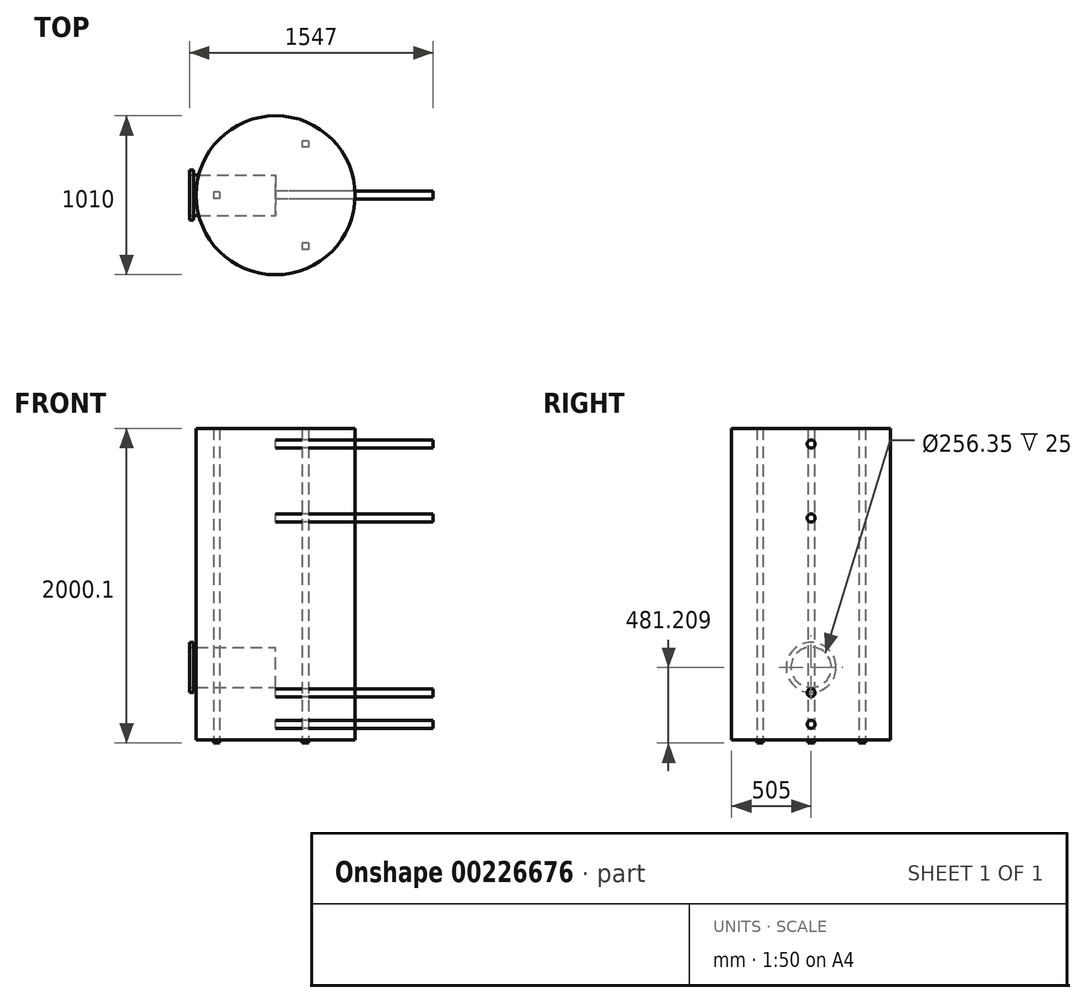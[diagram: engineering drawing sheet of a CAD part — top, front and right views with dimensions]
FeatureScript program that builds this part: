
annotation { "Feature Type Name" : "Feature", "Feature Type Description" : "" }
export const myFeature = defineFeature(function(context is Context, id is Id, definition is map)
    precondition{}
    {
        {
            var Q0;
            Q0=qCreatedBy(makeId("Top.planeOp"),FACE);
            var sketch = newSketch(context, id + "F0", { "sketchPlane" : qUnion([Q0])});
            skCircle(sketch, "E0", {"center": v(0, 0) * mm, "radius": 505 * mm});
            skPoint(sketch, "E1.0.midPoint", {"position": v(-93.82, -162.5) * mm});
            skLineSegment(sketch, "E2.bottom", {"start": v(207.64, -305) * mm, "end": v(167.64, -305) * mm});
            skLineSegment(sketch, "E2.top", {"start": v(207.64, -345) * mm, "end": v(167.64, -345) * mm});
            skLineSegment(sketch, "E2.left", {"start": v(207.64, -305) * mm, "end": v(207.64, -345) * mm});
            skLineSegment(sketch, "E2.right", {"start": v(167.64, -305) * mm, "end": v(167.64, -345) * mm});
            skPoint(sketch, "E2.middle", {"position": v(187.64, -325) * mm});
            skLineSegment(sketch, "E3.bottom", {"start": v(207.64, 345) * mm, "end": v(167.64, 345) * mm});
            skLineSegment(sketch, "E3.top", {"start": v(207.64, 305) * mm, "end": v(167.64, 305) * mm});
            skLineSegment(sketch, "E3.left", {"start": v(207.64, 345) * mm, "end": v(207.64, 305) * mm});
            skLineSegment(sketch, "E3.right", {"start": v(167.64, 345) * mm, "end": v(167.64, 305) * mm});
            skPoint(sketch, "E3.middle", {"position": v(187.64, 325) * mm});
            skLineSegment(sketch, "E4.bottom", {"start": v(-355.28, 20) * mm, "end": v(-395.28, 20) * mm});
            skLineSegment(sketch, "E4.top", {"start": v(-355.28, -20) * mm, "end": v(-395.28, -20) * mm});
            skLineSegment(sketch, "E4.left", {"start": v(-355.28, 20) * mm, "end": v(-355.28, -20) * mm});
            skLineSegment(sketch, "E4.right", {"start": v(-395.28, 20) * mm, "end": v(-395.28, -20) * mm});
            skPoint(sketch, "E4.middle", {"position": v(-375.28, 0) * mm});
            skSolve(sketch);
        }
        {
            var Q0;
            Q0=makeQuery(id+"F0.imprint","IMPRINT",FACE,{"disambiguationData":[TD([[makeQuery(id+"F0.imprint","IMPRINT",EDGE,{"derivedFrom":sQuery(id+"F0.wireOp",EDGE,"E0")}),1.0]])]});
            extrude(context, id + "F1", {"entities" : qUnion([Q0]), "depth" : 1980 * mm});
        }
        {
            var Q0;
            Q0=qCreatedBy(makeId("Right.planeOp"),FACE);
            var sketch = newSketch(context, id + "F2", { "sketchPlane" : qUnion([Q0])});
            skLineSegment(sketch, "E5", {"start": v(0, 0) * mm, "end": v(0, 100) * mm});
            skLineSegment(sketch, "E6", {"start": v(0, 100) * mm, "end": v(0, 300) * mm});
            skLineSegment(sketch, "E7", {"start": v(0, 300) * mm, "end": v(0, 1410) * mm});
            skLineSegment(sketch, "E8", {"start": v(0, 1410) * mm, "end": v(0, 1880) * mm});
            skCircle(sketch, "E9", {"center": v(0, 100) * mm, "radius": 25.4 * mm});
            skCircle(sketch, "E10", {"center": v(0, 300) * mm, "radius": 25.4 * mm});
            skCircle(sketch, "E11", {"center": v(0, 1410) * mm, "radius": 25.4 * mm});
            skCircle(sketch, "E12", {"center": v(0, 1880) * mm, "radius": 25.4 * mm});
            skCircle(sketch, "E13", {"center": v(0, 554.63) * mm, "radius": 129.58 * mm});
            skSolve(sketch);
        }
        {
            var Q0;
            {var subQ0=sQuery(id+"F2.wireOp",EDGE,"E6");var subQ1=sQuery(id+"F2.wireOp",EDGE,"E5");var subQ2=makeQuery(id+"F2.imprint","INTERSECT",VERTEX,{"derivedFrom":[subQ1,subQ0]});Q0=makeQuery(id+"F2.imprint","IMPRINT",FACE,{"disambiguationData":[TD([[makeQuery(id+"F2.imprint","IMPRINT",EDGE,{"disambiguationData":[TD([[subQ2,1.0]])],"derivedFrom":subQ1}),1.0]])]});}
            var Q1;
            {var subQ0=sQuery(id+"F2.wireOp",EDGE,"E6");var subQ1=sQuery(id+"F2.wireOp",EDGE,"E5");var subQ2=makeQuery(id+"F2.imprint","INTERSECT",VERTEX,{"derivedFrom":[subQ1,subQ0]});Q1=makeQuery(id+"F2.imprint","IMPRINT",FACE,{"disambiguationData":[TD([[makeQuery(id+"F2.imprint","IMPRINT",EDGE,{"disambiguationData":[TD([[subQ2,1.0]])],"derivedFrom":subQ1}),-1.0]])]});}
            var Q2;
            {var subQ0=sQuery(id+"F2.wireOp",EDGE,"E7");var subQ1=sQuery(id+"F2.wireOp",EDGE,"E6");var subQ2=makeQuery(id+"F2.imprint","INTERSECT",VERTEX,{"derivedFrom":[subQ1,subQ0]});Q2=makeQuery(id+"F2.imprint","IMPRINT",FACE,{"disambiguationData":[TD([[makeQuery(id+"F2.imprint","IMPRINT",EDGE,{"disambiguationData":[TD([[subQ2,1.0]])],"derivedFrom":subQ1}),1.0]])]});}
            var Q3;
            {var subQ0=sQuery(id+"F2.wireOp",EDGE,"E7");var subQ1=sQuery(id+"F2.wireOp",EDGE,"E6");var subQ2=makeQuery(id+"F2.imprint","INTERSECT",VERTEX,{"derivedFrom":[subQ1,subQ0]});Q3=makeQuery(id+"F2.imprint","IMPRINT",FACE,{"disambiguationData":[TD([[makeQuery(id+"F2.imprint","IMPRINT",EDGE,{"disambiguationData":[TD([[subQ2,1.0]])],"derivedFrom":subQ1}),-1.0]])]});}
            var Q4;
            {var subQ0=sQuery(id+"F2.wireOp",EDGE,"E8");var subQ1=sQuery(id+"F2.wireOp",EDGE,"E7");var subQ2=makeQuery(id+"F2.imprint","INTERSECT",VERTEX,{"derivedFrom":[subQ1,subQ0]});Q4=makeQuery(id+"F2.imprint","IMPRINT",FACE,{"disambiguationData":[TD([[makeQuery(id+"F2.imprint","IMPRINT",EDGE,{"disambiguationData":[TD([[subQ2,1.0]])],"derivedFrom":subQ1}),1.0]])]});}
            var Q5;
            {var subQ0=sQuery(id+"F2.wireOp",EDGE,"E8");var subQ1=sQuery(id+"F2.wireOp",EDGE,"E7");var subQ2=makeQuery(id+"F2.imprint","INTERSECT",VERTEX,{"derivedFrom":[subQ1,subQ0]});Q5=makeQuery(id+"F2.imprint","IMPRINT",FACE,{"disambiguationData":[TD([[makeQuery(id+"F2.imprint","IMPRINT",EDGE,{"disambiguationData":[TD([[subQ2,1.0]])],"derivedFrom":subQ1}),-1.0]])]});}
            var Q6;
            Q6=makeQuery(id+"F2.imprint","IMPRINT",FACE,{"disambiguationData":[TD([[makeQuery(id+"F2.imprint","IMPRINT",EDGE,{"derivedFrom":sQuery(id+"F2.wireOp",EDGE,"E12")}),1.0]])]});
            extrude(context, id + "F3", {"entities" : qUnion([Q0, Q1, Q2, Q3, Q4, Q5, Q6]), "depth" : 1000 * mm});
        }
        {
            var Q0;
            Q0=makeQuery(id+"F1.opExtrude","CAP_FACE",FACE,{"disambiguationData":[OSD([sQuery(id+"F0.wireOp",EDGE,"E0"),sQuery(id+"F0.wireOp",EDGE,"E2.bottom"),sQuery(id+"F0.wireOp",EDGE,"E2.top"),sQuery(id+"F0.wireOp",EDGE,"E2.left"),sQuery(id+"F0.wireOp",EDGE,"E2.right"),sQuery(id+"F0.wireOp",EDGE,"E3.bottom"),sQuery(id+"F0.wireOp",EDGE,"E3.top"),sQuery(id+"F0.wireOp",EDGE,"E3.left"),sQuery(id+"F0.wireOp",EDGE,"E3.right"),sQuery(id+"F0.wireOp",EDGE,"E4.bottom"),sQuery(id+"F0.wireOp",EDGE,"E4.top"),sQuery(id+"F0.wireOp",EDGE,"E4.left"),sQuery(id+"F0.wireOp",EDGE,"E4.right")])],"isStart":true});
            var sketch = newSketch(context, id + "F4", { "sketchPlane" : qUnion([Q0])});
            skLineSegment(sketch, "E14.bottom", {"start": v(-395.28, 20) * mm, "end": v(-355.28, 20) * mm});
            skLineSegment(sketch, "E14.top", {"start": v(-395.28, -20) * mm, "end": v(-355.28, -20) * mm});
            skLineSegment(sketch, "E14.left", {"start": v(-395.28, 20) * mm, "end": v(-395.28, -20) * mm});
            skLineSegment(sketch, "E14.right", {"start": v(-355.28, 20) * mm, "end": v(-355.28, -20) * mm});
            skLineSegment(sketch, "E15.bottom", {"start": v(167.64, -305) * mm, "end": v(207.64, -305) * mm});
            skLineSegment(sketch, "E15.top", {"start": v(167.64, -345) * mm, "end": v(207.64, -345) * mm});
            skLineSegment(sketch, "E15.left", {"start": v(167.64, -305) * mm, "end": v(167.64, -345) * mm});
            skLineSegment(sketch, "E15.right", {"start": v(207.64, -305) * mm, "end": v(207.64, -345) * mm});
            skLineSegment(sketch, "E16.bottom", {"start": v(167.64, 345) * mm, "end": v(207.64, 345) * mm});
            skLineSegment(sketch, "E16.top", {"start": v(167.64, 305) * mm, "end": v(207.64, 305) * mm});
            skLineSegment(sketch, "E16.left", {"start": v(167.64, 345) * mm, "end": v(167.64, 305) * mm});
            skLineSegment(sketch, "E16.right", {"start": v(207.64, 345) * mm, "end": v(207.64, 305) * mm});
            skSolve(sketch);
        }
        {
            var Q0;
            Q0=makeQuery(id+"F4.imprint","IMPRINT",FACE,{"disambiguationData":[TD([[makeQuery(id+"F4.imprint","IMPRINT",EDGE,{"derivedFrom":sQuery(id+"F4.wireOp",EDGE,"E16.bottom")}),1.0]])]});
            var Q1;
            Q1=makeQuery(id+"F4.imprint","IMPRINT",FACE,{"disambiguationData":[TD([[makeQuery(id+"F4.imprint","IMPRINT",EDGE,{"derivedFrom":sQuery(id+"F4.wireOp",EDGE,"E14.bottom")}),1.0]])]});
            var Q2;
            Q2=makeQuery(id+"F4.imprint","IMPRINT",FACE,{"disambiguationData":[TD([[makeQuery(id+"F4.imprint","IMPRINT",EDGE,{"derivedFrom":sQuery(id+"F4.wireOp",EDGE,"E15.bottom")}),1.0]])]});
            extrude(context, id + "F5", {"entities" : qUnion([Q0, Q1, Q2]), "depth" : 20 * mm});
        }
        {
            var Q0;
            Q0=makeQuery(id+"F1.opExtrude","CAP_FACE",FACE,{"disambiguationData":[OSD([sQuery(id+"F0.wireOp",EDGE,"E0"),sQuery(id+"F0.wireOp",EDGE,"E2.bottom"),sQuery(id+"F0.wireOp",EDGE,"E2.top"),sQuery(id+"F0.wireOp",EDGE,"E2.left"),sQuery(id+"F0.wireOp",EDGE,"E2.right"),sQuery(id+"F0.wireOp",EDGE,"E3.bottom"),sQuery(id+"F0.wireOp",EDGE,"E3.top"),sQuery(id+"F0.wireOp",EDGE,"E3.left"),sQuery(id+"F0.wireOp",EDGE,"E3.right"),sQuery(id+"F0.wireOp",EDGE,"E4.bottom"),sQuery(id+"F0.wireOp",EDGE,"E4.top"),sQuery(id+"F0.wireOp",EDGE,"E4.left"),sQuery(id+"F0.wireOp",EDGE,"E4.right")])],"isStart":false});
            var sketch = newSketch(context, id + "F6", { "sketchPlane" : qUnion([Q0])});
            skCircle(sketch, "E17", {"center": v(0, 0) * mm, "radius": 505 * mm});
            skSolve(sketch);
        }
        {
            var Q0;
            Q0 = qSketchRegion(id + "F6", true);
            extrude(context, id + "F7", {"entities" : qUnion([Q0]), "operationType" : NewBodyOperationType.ADD, "depth" : 0.1 * mm});
        }
        {
            var Q0;
            Q0=qCreatedBy(makeId("Right.planeOp"),FACE);
            var sketch = newSketch(context, id + "F8", { "sketchPlane" : qUnion([Q0])});
            skCircle(sketch, "E18", {"center": v(0, 461.2) * mm, "radius": 128.17 * mm});
            skSolve(sketch);
        }
        {
            var Q0;
            Q0=makeQuery(id+"F8.imprint","IMPRINT",FACE,{"disambiguationData":[TD([[makeQuery(id+"F8.imprint","IMPRINT",EDGE,{"derivedFrom":sQuery(id+"F8.wireOp",EDGE,"E18")}),1.0]])]});
            extrude(context, id + "F9", {"entities" : qUnion([Q0]), "oppositeDirection" : true, "depth" : 522 * mm});
        }
        {
            var Q0;
            Q0=makeQuery(id+"F9.opExtrude","CAP_FACE",FACE,{"disambiguationData":[OSD([sQuery(id+"F8.wireOp",EDGE,"E18")])],"isStart":false});
            var sketch = newSketch(context, id + "F10", { "sketchPlane" : qUnion([Q0])});
            skCircle(sketch, "E19", {"center": v(0, 461.2) * mm, "radius": 158.86 * mm});
            skSolve(sketch);
        }
        {
            var Q0;
            Q0=makeQuery(id+"F10.imprint","IMPRINT",FACE,{"disambiguationData":[TD([[makeQuery(id+"F10.imprint","IMPRINT",EDGE,{"derivedFrom":sQuery(id+"F10.wireOp",EDGE,"E19")}),1.0]])]});
            extrude(context, id + "F11", {"entities" : qUnion([Q0]), "depth" : 25 * mm});
        }
    });
